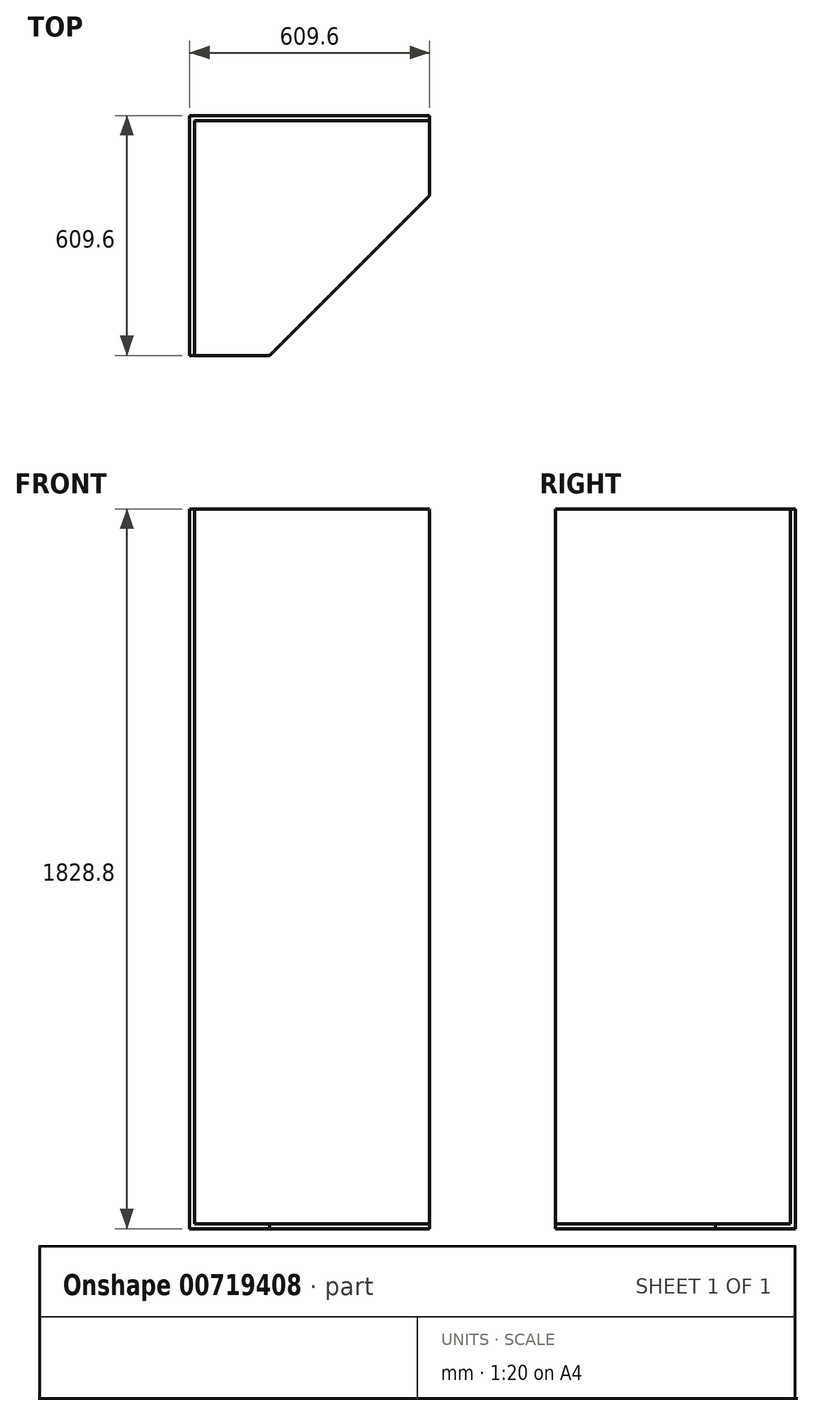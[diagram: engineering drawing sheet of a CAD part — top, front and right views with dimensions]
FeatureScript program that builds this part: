
annotation { "Feature Type Name" : "Feature", "Feature Type Description" : "" }
export const myFeature = defineFeature(function(context is Context, id is Id, definition is map)
    precondition{}
    {
        {
            var Q0;
            Q0=qCreatedBy(makeId("Front.planeOp"),FACE);
            var sketch = newSketch(context, id + "F0", { "sketchPlane" : qUnion([Q0])});
            skLineSegment(sketch, "E0.bottom", {"start": v(0, 1000.2) * mm, "end": v(609.6, 1000.2) * mm});
            skLineSegment(sketch, "E0.top", {"start": v(0, -828.6) * mm, "end": v(609.6, -828.6) * mm});
            skLineSegment(sketch, "E0.left", {"start": v(0, 1000.2) * mm, "end": v(0, -828.6) * mm});
            skLineSegment(sketch, "E0.right", {"start": v(609.6, 1000.2) * mm, "end": v(609.6, -828.6) * mm});
            skSolve(sketch);
        }
        {
            var Q0;
            Q0 = qSketchRegion(id + "F0", true);
            extrude(context, id + "F1", {"entities" : qUnion([Q0]), "depth" : 12.7 * mm, "offsetDistance" : 25.4 * mm});
        }
        {
            var Q0;
            Q0=makeQuery(id+"F1.opExtrude","CAP_EDGE",EDGE,{"disambiguationData":[OSD([sQuery(id+"F0.wireOp",EDGE,"E0.left")])],"isStart":false});
            chamfer(context, id + "F2", {"entities" : qUnion([Q0]), "width" : 12.7 * mm, "tangentPropagation" : true});
        }
        {
            var Q0;
            Q0=makeQuery(id+"F1.opExtrude","SWEPT_BODY",BODY,{"disambiguationData":[OSD([sQuery(id+"F0.wireOp",EDGE,"E0.bottom"),sQuery(id+"F0.wireOp",EDGE,"E0.top"),sQuery(id+"F0.wireOp",EDGE,"E0.left"),sQuery(id+"F0.wireOp",EDGE,"E0.right")])]});
            var Q1;
            Q1=makeQuery(id+"F2.opChamfer","BLEND_FACE",FACE,{"disambiguationData":[OSD([sQuery(id+"F0.wireOp",EDGE,"E0.left")])]});
            mirror(context, id + "F3", {"operationType" : NewBodyOperationType.ADD, "entities" : qUnion([Q0]), "mirrorPlane" : qUnion([Q1])});
        }
        {
            var Q0;
            {var subQ0=makeQuery(id+"F1.opExtrude","SWEPT_FACE",FACE,{"disambiguationData":[OSD([sQuery(id+"F0.wireOp",EDGE,"E0.top")])]});Q0=makeQuery(id+"F3.boolean.opBoolean","MERGE",FACE,{"derivedFrom":[subQ0,makeQuery(id+"F3.opPattern","COPY",FACE,{"derivedFrom":subQ0,"instanceName":"1"})]});}
            var sketch = newSketch(context, id + "F4", { "sketchPlane" : qUnion([Q0])});
            skLineSegment(sketch, "E1.bottom", {"start": v(12.7, 12.7) * mm, "end": v(609.6, 12.7) * mm});
            skLineSegment(sketch, "E1.top", {"start": v(12.7, 609.6) * mm, "end": v(609.6, 609.6) * mm});
            skLineSegment(sketch, "E1.left", {"start": v(12.7, 12.7) * mm, "end": v(12.7, 609.6) * mm});
            skLineSegment(sketch, "E1.right", {"start": v(609.6, 12.7) * mm, "end": v(609.6, 609.6) * mm});
            skSolve(sketch);
        }
        {
            var Q0;
            Q0 = qSketchRegion(id + "F4", true);
            extrude(context, id + "F5", {"entities" : qUnion([Q0]), "operationType" : NewBodyOperationType.ADD, "depth" : -12.7 * mm, "offsetDistance" : 25.4 * mm});
        }
        {
            var Q0;
            Q0=makeQuery(id+"F5.opExtrude","SWEPT_EDGE",EDGE,{"disambiguationData":[OSD([sQuery(id+"F4.wireOp",EDGE,"E1.top"),sQuery(id+"F4.wireOp",EDGE,"E1.right")])]});
            chamfer(context, id + "F6", {"entities" : qUnion([Q0]), "width" : 406.4 * mm, "tangentPropagation" : true});
        }
    });
